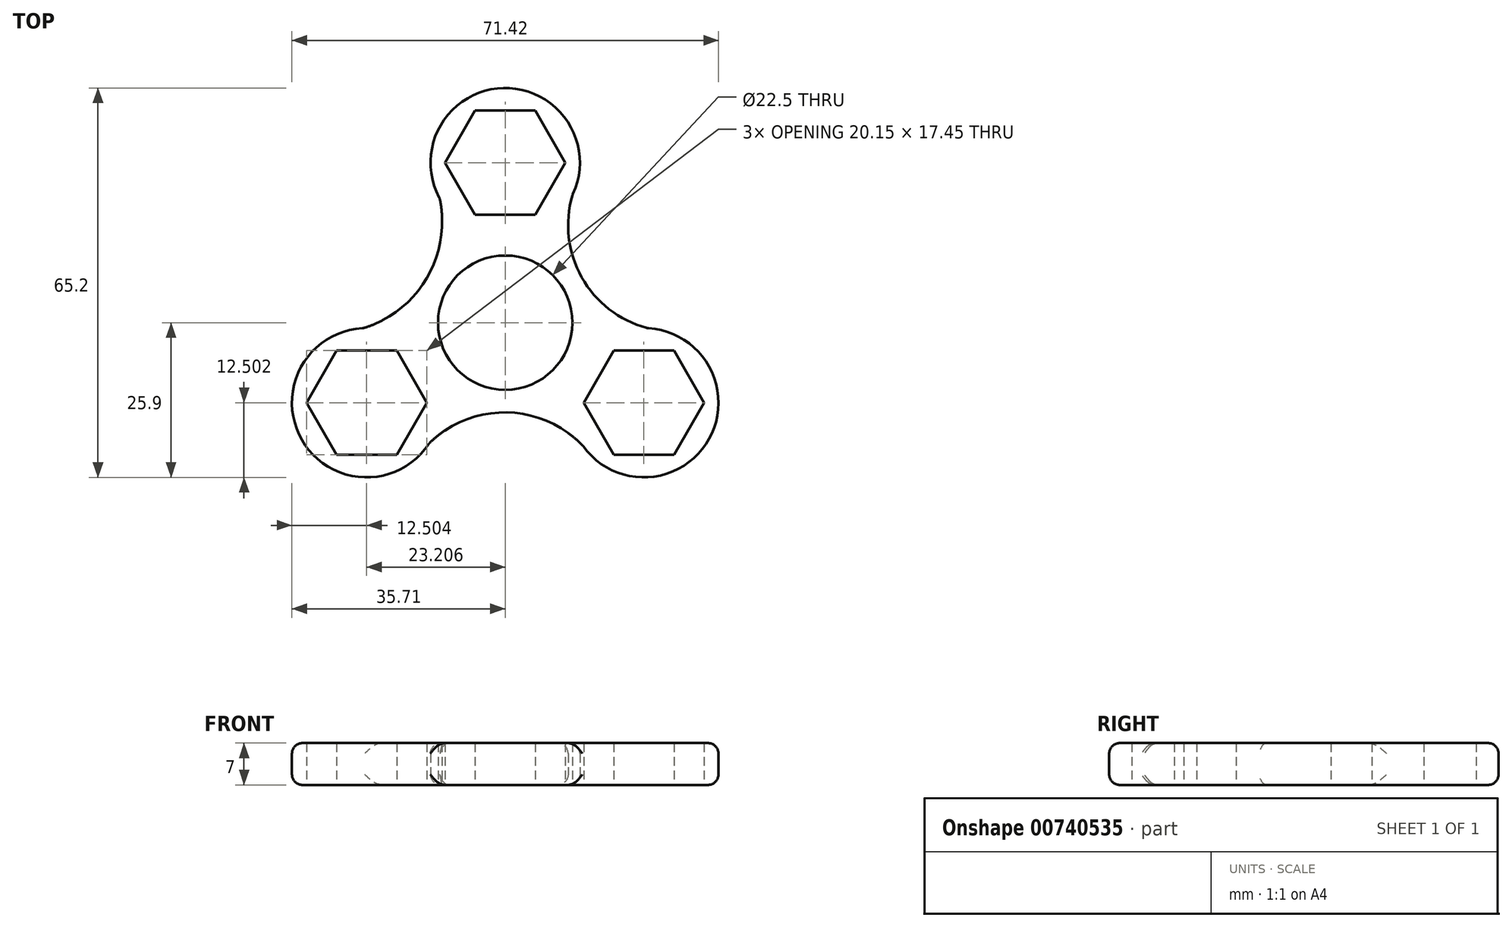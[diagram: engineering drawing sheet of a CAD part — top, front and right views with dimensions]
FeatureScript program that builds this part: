
annotation { "Feature Type Name" : "Feature", "Feature Type Description" : "" }
export const myFeature = defineFeature(function(context is Context, id is Id, definition is map)
    precondition{}
    {
        {
            var Q0;
            Q0=qCreatedBy(makeId("Top.planeOp"),FACE);
            var sketch = newSketch(context, id + "F0", { "sketchPlane" : qUnion([Q0])});
            skCircle(sketch, "E0", {"center": v(0, 0) * mm, "radius": 11.25 * mm});
            skCircle(sketch, "E1.cCircle", {"center": v(0, 26.8) * mm, "radius": 8.72 * mm, "construction": true});
            skLineSegment(sketch, "E1.0", {"start": v(5.04, 35.52) * mm, "end": v(10.07, 26.8) * mm});
            skLineSegment(sketch, "E1.1", {"start": v(10.07, 26.8) * mm, "end": v(5.04, 18.07) * mm});
            skLineSegment(sketch, "E1.2", {"start": v(5.04, 18.07) * mm, "end": v(-5.04, 18.07) * mm});
            skLineSegment(sketch, "E1.3", {"start": v(-5.04, 18.07) * mm, "end": v(-10.07, 26.8) * mm});
            skLineSegment(sketch, "E1.4", {"start": v(-10.07, 26.8) * mm, "end": v(-5.04, 35.52) * mm});
            skLineSegment(sketch, "E1.5", {"start": v(-5.04, 35.52) * mm, "end": v(5.04, 35.52) * mm});
            skPoint(sketch, "E1.0.midPoint", {"position": v(7.56, 31.16) * mm});
            skArc(sketch, "E2", {"start": v(11.3, 21.44) * mm, "mid": v(-0.37, 39.3) * mm, "end": v(-10.96, 20.78) * mm});
            skLineSegment(sketch, "E3.1.0", {"start": v(-18.17, -22.12) * mm, "end": v(-28.24, -22.12) * mm});
            skLineSegment(sketch, "E3.1.1", {"start": v(-28.24, -22.12) * mm, "end": v(-33.28, -13.4) * mm});
            skLineSegment(sketch, "E3.1.2", {"start": v(-33.28, -13.4) * mm, "end": v(-28.24, -4.67) * mm});
            skLineSegment(sketch, "E3.1.3", {"start": v(-28.24, -4.67) * mm, "end": v(-18.17, -4.67) * mm});
            skLineSegment(sketch, "E3.1.4", {"start": v(-18.17, -4.67) * mm, "end": v(-13.13, -13.4) * mm});
            skLineSegment(sketch, "E3.1.5", {"start": v(-13.13, -13.4) * mm, "end": v(-18.17, -22.12) * mm});
            skArc(sketch, "E3.1.6", {"start": v(-23.73, -0.9) * mm, "mid": v(-34.05, -19.62) * mm, "end": v(-12.7, -20.16) * mm});
            skLineSegment(sketch, "E3.2.0", {"start": v(28.24, -4.67) * mm, "end": v(33.28, -13.4) * mm});
            skLineSegment(sketch, "E3.2.1", {"start": v(33.28, -13.4) * mm, "end": v(28.24, -22.12) * mm});
            skLineSegment(sketch, "E3.2.2", {"start": v(28.24, -22.12) * mm, "end": v(18.17, -22.12) * mm});
            skLineSegment(sketch, "E3.2.3", {"start": v(18.17, -22.12) * mm, "end": v(13.13, -13.4) * mm});
            skLineSegment(sketch, "E3.2.4", {"start": v(13.13, -13.4) * mm, "end": v(18.17, -4.67) * mm});
            skLineSegment(sketch, "E3.2.5", {"start": v(18.17, -4.67) * mm, "end": v(28.24, -4.67) * mm});
            skArc(sketch, "E3.2.6", {"start": v(13, -20.62) * mm, "mid": v(34.16, -19.42) * mm, "end": v(23.85, -0.91) * mm});
            skArc(sketch, "E4", {"start": v(11.3, 21.44) * mm, "mid": v(12.82, 7.6) * mm, "end": v(23.85, -0.91) * mm});
            skArc(sketch, "E5", {"start": v(13, -20.62) * mm, "mid": v(0.25, -15.02) * mm, "end": v(-12.7, -20.16) * mm});
            skArc(sketch, "E6", {"start": v(-23.73, -0.9) * mm, "mid": v(-13.14, 7.47) * mm, "end": v(-10.96, 20.78) * mm});
            skSolve(sketch);
        }
        {
            var Q0;
            {var subQ0=sQuery(id+"F0.wireOp",EDGE,"uxgLeyJD-YWfx-X5wX-Qh6I-GeaC6sstPdhc");var subQ1=sQuery(id+"F0.wireOp",EDGE,"77fc6f8a-58b6-4ae2-93e2-5267b44f56bd.0");var subQ2=makeQuery(id+"F0.imprint","INTERSECT",VERTEX,{"disambiguationData":[OD(1.0)],"derivedFrom":[subQ1,subQ0]});Q0=makeQuery(id+"F0.imprint","IMPRINT",FACE,{"disambiguationData":[TD([[makeQuery(id+"F0.imprint","IMPRINT",EDGE,{"disambiguationData":[TD([[subQ2,-1.0]])],"derivedFrom":subQ1}),-1.0]])]});}
            var Q1;
            Q1=makeQuery(id+"F0.imprint","IMPRINT",FACE,{"disambiguationData":[TD([[makeQuery(id+"F0.imprint","IMPRINT",EDGE,{"derivedFrom":sQuery(id+"F0.wireOp",EDGE,"E0")}),-1.0]])]});
            var Q2;
            {var subQ0=sQuery(id+"F0.wireOp",EDGE,"uxgLeyJD-YWfx-X5wX-Qh6I-GeaC6sstPdhc");var subQ1=sQuery(id+"F0.wireOp",EDGE,"77fc6f8a-58b6-4ae2-93e2-5267b44f56bd.0");var subQ2=makeQuery(id+"F0.imprint","INTERSECT",VERTEX,{"disambiguationData":[OD(0.0)],"derivedFrom":[subQ1,subQ0]});Q2=makeQuery(id+"F0.imprint","IMPRINT",FACE,{"disambiguationData":[TD([[makeQuery(id+"F0.imprint","IMPRINT",EDGE,{"disambiguationData":[TD([[subQ2,1.0]])],"derivedFrom":subQ1}),-1.0]])]});}
            var Q3;
            Q3=makeQuery(id+"F0.imprint","IMPRINT",FACE,{"disambiguationData":[TD([[makeQuery(id+"F0.imprint","IMPRINT",EDGE,{"derivedFrom":sQuery(id+"F0.wireOp",EDGE,"E1.0")}),1.0]])]});
            var Q4;
            {var subQ0=sQuery(id+"F0.wireOp",EDGE,"meCCL5Ld-UqJw-OKnt-FaJc-FDM27yth5b5o");var subQ1=sQuery(id+"F0.wireOp",EDGE,"77fc6f8a-58b6-4ae2-93e2-5267b44f56bd.0");var subQ2=makeQuery(id+"F0.imprint","INTERSECT",VERTEX,{"disambiguationData":[OD(0.0)],"derivedFrom":[subQ1,subQ0]});Q4=makeQuery(id+"F0.imprint","IMPRINT",FACE,{"disambiguationData":[TD([[makeQuery(id+"F0.imprint","IMPRINT",EDGE,{"disambiguationData":[TD([[subQ2,-1.0]])],"derivedFrom":subQ1}),-1.0]])]});}
            var Q5;
            {var subQ0=sQuery(id+"F0.wireOp",EDGE,"meCCL5Ld-UqJw-OKnt-FaJc-FDM27yth5b5o");var subQ1=sQuery(id+"F0.wireOp",EDGE,"77fc6f8a-58b6-4ae2-93e2-5267b44f56bd.0");var subQ2=makeQuery(id+"F0.imprint","INTERSECT",VERTEX,{"disambiguationData":[OD(1.0)],"derivedFrom":[subQ1,subQ0]});Q5=makeQuery(id+"F0.imprint","IMPRINT",FACE,{"disambiguationData":[TD([[makeQuery(id+"F0.imprint","IMPRINT",EDGE,{"disambiguationData":[TD([[subQ2,1.0]])],"derivedFrom":subQ1}),-1.0]])]});}
            var Q6;
            Q6=makeQuery(id+"F0.imprint","IMPRINT",FACE,{"disambiguationData":[TD([[makeQuery(id+"F0.imprint","IMPRINT",EDGE,{"derivedFrom":sQuery(id+"F0.wireOp",EDGE,"E3.2.0")}),1.0]])]});
            var Q7;
            {var subQ0=sQuery(id+"F0.wireOp",EDGE,"G1T3lmNx-egao-C8Ap-W983-DwZWNCfD9i1M");var subQ1=sQuery(id+"F0.wireOp",EDGE,"77fc6f8a-58b6-4ae2-93e2-5267b44f56bd.0");var subQ2=makeQuery(id+"F0.imprint","INTERSECT",VERTEX,{"disambiguationData":[OD(1.0)],"derivedFrom":[subQ1,subQ0]});Q7=makeQuery(id+"F0.imprint","IMPRINT",FACE,{"disambiguationData":[TD([[makeQuery(id+"F0.imprint","IMPRINT",EDGE,{"disambiguationData":[TD([[subQ2,-1.0]])],"derivedFrom":subQ1}),-1.0]])]});}
            var Q8;
            {var subQ0=sQuery(id+"F0.wireOp",EDGE,"G1T3lmNx-egao-C8Ap-W983-DwZWNCfD9i1M");var subQ1=sQuery(id+"F0.wireOp",EDGE,"77fc6f8a-58b6-4ae2-93e2-5267b44f56bd.0");var subQ2=makeQuery(id+"F0.imprint","INTERSECT",VERTEX,{"disambiguationData":[OD(0.0)],"derivedFrom":[subQ1,subQ0]});Q8=makeQuery(id+"F0.imprint","IMPRINT",FACE,{"disambiguationData":[TD([[makeQuery(id+"F0.imprint","IMPRINT",EDGE,{"disambiguationData":[TD([[subQ2,1.0]])],"derivedFrom":subQ1}),-1.0]])]});}
            var Q9;
            Q9=makeQuery(id+"F0.imprint","IMPRINT",FACE,{"disambiguationData":[TD([[makeQuery(id+"F0.imprint","IMPRINT",EDGE,{"derivedFrom":sQuery(id+"F0.wireOp",EDGE,"E3.1.0")}),1.0]])]});
            var Q10;
            {var subQ0=sQuery(id+"F0.wireOp",EDGE,"E3.1.6");var subQ1=sQuery(id+"F0.wireOp",EDGE,"77fc6f8a-58b6-4ae2-93e2-5267b44f56bd.0");var subQ2=makeQuery(id+"F0.imprint","INTERSECT",VERTEX,{"disambiguationData":[OD(0.0)],"derivedFrom":[subQ1,subQ0]});Q10=makeQuery(id+"F0.imprint","IMPRINT",FACE,{"disambiguationData":[TD([[makeQuery(id+"F0.imprint","IMPRINT",EDGE,{"disambiguationData":[TD([[subQ2,-1.0]])],"derivedFrom":subQ1}),1.0]])]});}
            var Q11;
            {var subQ0=sQuery(id+"F0.wireOp",EDGE,"E3.2.6");var subQ1=sQuery(id+"F0.wireOp",EDGE,"77fc6f8a-58b6-4ae2-93e2-5267b44f56bd.0");var subQ2=makeQuery(id+"F0.imprint","INTERSECT",VERTEX,{"disambiguationData":[OD(0.0)],"derivedFrom":[subQ1,subQ0]});Q11=makeQuery(id+"F0.imprint","IMPRINT",FACE,{"disambiguationData":[TD([[makeQuery(id+"F0.imprint","IMPRINT",EDGE,{"disambiguationData":[TD([[subQ2,-1.0]])],"derivedFrom":subQ1}),1.0]])]});}
            var Q12;
            {var subQ0=sQuery(id+"F0.wireOp",EDGE,"E2");var subQ1=sQuery(id+"F0.wireOp",EDGE,"77fc6f8a-58b6-4ae2-93e2-5267b44f56bd.0");var subQ2=makeQuery(id+"F0.imprint","INTERSECT",VERTEX,{"disambiguationData":[OD(0.0)],"derivedFrom":[subQ1,subQ0]});Q12=makeQuery(id+"F0.imprint","IMPRINT",FACE,{"disambiguationData":[TD([[makeQuery(id+"F0.imprint","IMPRINT",EDGE,{"disambiguationData":[TD([[subQ2,-1.0]])],"derivedFrom":subQ1}),1.0]])]});}
            var Q13;
            {var subQ0=sQuery(id+"F0.wireOp",EDGE,"E6");var subQ1=sQuery(id+"F0.wireOp",EDGE,"77fc6f8a-58b6-4ae2-93e2-5267b44f56bd.0");var subQ2=makeQuery(id+"F0.imprint","INTERSECT",VERTEX,{"disambiguationData":[OD(0.0)],"derivedFrom":[subQ1,subQ0]});Q13=makeQuery(id+"F0.imprint","IMPRINT",FACE,{"disambiguationData":[TD([[makeQuery(id+"F0.imprint","IMPRINT",EDGE,{"disambiguationData":[TD([[subQ2,1.0]])],"derivedFrom":subQ1}),-1.0]])]});}
            var Q14;
            {var subQ0=sQuery(id+"F0.wireOp",EDGE,"E4");var subQ1=sQuery(id+"F0.wireOp",EDGE,"77fc6f8a-58b6-4ae2-93e2-5267b44f56bd.0");var subQ2=makeQuery(id+"F0.imprint","INTERSECT",VERTEX,{"disambiguationData":[OD(0.0)],"derivedFrom":[subQ1,subQ0]});Q14=makeQuery(id+"F0.imprint","IMPRINT",FACE,{"disambiguationData":[TD([[makeQuery(id+"F0.imprint","IMPRINT",EDGE,{"disambiguationData":[TD([[subQ2,-1.0]])],"derivedFrom":subQ1}),-1.0]])]});}
            var Q15;
            {var subQ0=sQuery(id+"F0.wireOp",EDGE,"E6");var subQ1=sQuery(id+"F0.wireOp",EDGE,"77fc6f8a-58b6-4ae2-93e2-5267b44f56bd.0");var subQ2=makeQuery(id+"F0.imprint","INTERSECT",VERTEX,{"disambiguationData":[OD(1.0)],"derivedFrom":[subQ1,subQ0]});Q15=makeQuery(id+"F0.imprint","IMPRINT",FACE,{"disambiguationData":[TD([[makeQuery(id+"F0.imprint","IMPRINT",EDGE,{"disambiguationData":[TD([[subQ2,-1.0]])],"derivedFrom":subQ1}),-1.0]])]});}
            var Q16;
            {var subQ0=sQuery(id+"F0.wireOp",EDGE,"E5");var subQ1=sQuery(id+"F0.wireOp",EDGE,"77fc6f8a-58b6-4ae2-93e2-5267b44f56bd.0");var subQ2=makeQuery(id+"F0.imprint","INTERSECT",VERTEX,{"disambiguationData":[OD(0.0)],"derivedFrom":[subQ1,subQ0]});Q16=makeQuery(id+"F0.imprint","IMPRINT",FACE,{"disambiguationData":[TD([[makeQuery(id+"F0.imprint","IMPRINT",EDGE,{"disambiguationData":[TD([[subQ2,1.0]])],"derivedFrom":subQ1}),-1.0]])]});}
            var Q17;
            {var subQ0=sQuery(id+"F0.wireOp",EDGE,"E5");var subQ1=sQuery(id+"F0.wireOp",EDGE,"77fc6f8a-58b6-4ae2-93e2-5267b44f56bd.0");var subQ2=makeQuery(id+"F0.imprint","INTERSECT",VERTEX,{"disambiguationData":[OD(1.0)],"derivedFrom":[subQ1,subQ0]});Q17=makeQuery(id+"F0.imprint","IMPRINT",FACE,{"disambiguationData":[TD([[makeQuery(id+"F0.imprint","IMPRINT",EDGE,{"disambiguationData":[TD([[subQ2,-1.0]])],"derivedFrom":subQ1}),-1.0]])]});}
            var Q18;
            {var subQ0=sQuery(id+"F0.wireOp",EDGE,"E4");var subQ1=sQuery(id+"F0.wireOp",EDGE,"77fc6f8a-58b6-4ae2-93e2-5267b44f56bd.0");var subQ2=makeQuery(id+"F0.imprint","INTERSECT",VERTEX,{"disambiguationData":[OD(1.0)],"derivedFrom":[subQ1,subQ0]});Q18=makeQuery(id+"F0.imprint","IMPRINT",FACE,{"disambiguationData":[TD([[makeQuery(id+"F0.imprint","IMPRINT",EDGE,{"disambiguationData":[TD([[subQ2,1.0]])],"derivedFrom":subQ1}),-1.0]])]});}
            extrude(context, id + "F1", {"entities" : qUnion([Q0, Q1, Q2, Q3, Q4, Q5, Q6, Q7, Q8, Q9, Q10, Q11, Q12, Q13, Q14, Q15, Q16, Q17, Q18]), "depth" : 7 * mm, "offsetDistance" : 25 * mm});
        }
        {
            var Q0;
            Q0=makeQuery(id+"F1.opExtrude","SWEPT_FACE",FACE,{"disambiguationData":[OSD([sQuery(id+"F0.wireOp",EDGE,"E3.2.6")])]});
            var Q1;
            Q1=makeQuery(id+"F1.opExtrude","SWEPT_FACE",FACE,{"disambiguationData":[OSD([sQuery(id+"F0.wireOp",EDGE,"E4")])]});
            var Q2;
            Q2=makeQuery(id+"F1.opExtrude","SWEPT_FACE",FACE,{"disambiguationData":[OSD([sQuery(id+"F0.wireOp",EDGE,"E2")])]});
            var Q3;
            Q3=makeQuery(id+"F1.opExtrude","SWEPT_FACE",FACE,{"disambiguationData":[OSD([sQuery(id+"F0.wireOp",EDGE,"E3.1.6")])]});
            fillet(context, id + "F2", {"entities" : qUnion([Q0, Q1, Q2, Q3]), "radius" : 1.75 * mm, "tangentPropagation" : true, "allowEdgeOverflow" : false});
        }
    });
